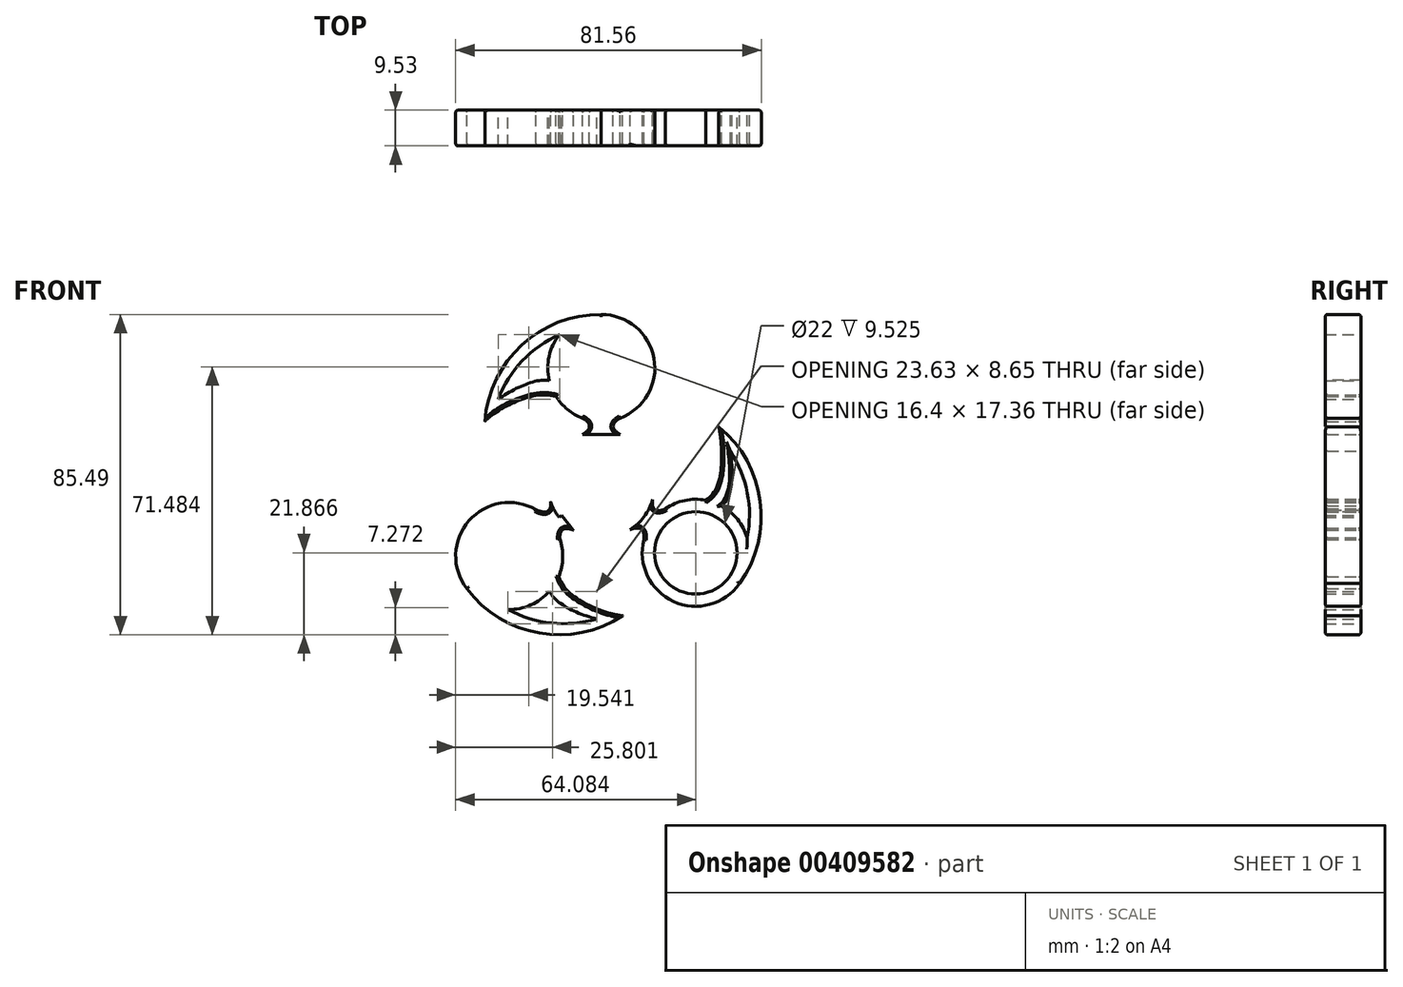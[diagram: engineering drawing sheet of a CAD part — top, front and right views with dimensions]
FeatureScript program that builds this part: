
annotation { "Feature Type Name" : "Feature", "Feature Type Description" : "" }
export const myFeature = defineFeature(function(context is Context, id is Id, definition is map)
    precondition{}
    {
        {
            var Q0;
            Q0=qCreatedBy(makeId("Front.planeOp"),FACE);
            var sketch = newSketch(context, id + "F0", { "sketchPlane" : qUnion([Q0])});
            skCircle(sketch, "E0", {"center": v(0, 0) * mm, "radius": 14.29 * mm});
            skLineSegment(sketch, "E1", {"start": v(0, 0) * mm, "end": v(0, 14.29) * mm});
            skLineSegment(sketch, "E2", {"start": v(0, 0) * mm, "end": v(-11.3, -8.76) * mm});
            skLineSegment(sketch, "E3", {"start": v(0, 0) * mm, "end": v(11.43, -8.57) * mm});
            skCircle(sketch, "E4", {"center": v(0, 31.12) * mm, "radius": 14.29 * mm});
            skLineSegment(sketch, "E5", {"start": v(0, 14.29) * mm, "end": v(0, 16.83) * mm});
            skArc(sketch, "E6", {"start": v(0, 45.4) * mm, "mid": v(-21.2, 37.27) * mm, "end": v(-31.1, 16.83) * mm});
            skFitSpline(sketch, "E7", {"points": [v(-31.1, 16.83) * mm, v(-17.35, 23.79) * mm, v(0, 16.83) * mm], "startDerivative": vector(18.3, 19.68) * mm, "endDerivative": vector(52.34, -33.11) * mm});
            skLineSegment(sketch, "E8", {"start": v(0, 15.56) * mm, "end": v(-3.18, 15.56) * mm});
            skPoint(sketch, "E8.endSnap0", {"position": v(0, 15.56) * mm});
            skLineSegment(sketch, "E9", {"start": v(0, 15.56) * mm, "end": v(3.18, 15.56) * mm});
            skLineSegment(sketch, "E10", {"start": v(0, 17.74) * mm, "end": v(5.03, 17.74) * mm});
            skLineSegment(sketch, "E11", {"start": v(0, 17.74) * mm, "end": v(-5.03, 17.74) * mm});
            skLineSegment(sketch, "E12", {"start": v(0, 14.29) * mm, "end": v(0, 13.37) * mm});
            skLineSegment(sketch, "E13", {"start": v(0, 13.37) * mm, "end": v(-5.03, 13.37) * mm});
            skLineSegment(sketch, "E14", {"start": v(0, 13.37) * mm, "end": v(5.03, 13.37) * mm});
            skFitSpline(sketch, "E15", {"points": [v(-5.03, 17.74) * mm, v(-3.18, 15.56) * mm, v(-5.03, 13.37) * mm], "startDerivative": vector(7.47, -4.37) * mm, "endDerivative": vector(-7.47, -4.37) * mm});
            skFitSpline(sketch, "E16", {"points": [v(5.03, 13.37) * mm, v(3.18, 15.56) * mm, v(5.03, 17.74) * mm], "startDerivative": vector(-7.47, 4.37) * mm, "endDerivative": vector(7.47, 4.37) * mm});
            skArc(sketch, "E17", {"start": v(4.36, 42.56) * mm, "mid": v(-16.61, 36.94) * mm, "end": v(-28.69, 18.9) * mm});
            skFitSpline(sketch, "E18", {"points": [v(-30.7, 19.98) * mm, v(-16.8, 27.72) * mm, v(0.44, 19.97) * mm], "startDerivative": vector(18.3, 19.68) * mm, "endDerivative": vector(52.34, -33.11) * mm});
            skLineSegment(sketch, "E19", {"start": v(-3.18, 15.56) * mm, "end": v(0, 14.29) * mm});
            skLineSegment(sketch, "E20", {"start": v(0, 14.29) * mm, "end": v(3.18, 15.56) * mm});
            skCircle(sketch, "E21", {"center": v(25.21, -18.22) * mm, "radius": 14.29 * mm});
            skLineSegment(sketch, "E22", {"start": v(11.43, -8.57) * mm, "end": v(13.51, -10.03) * mm});
            skArc(sketch, "E23", {"start": v(36.92, -26.42) * mm, "mid": v(42.42, -4.39) * mm, "end": v(31.34, 15.44) * mm});
            skFitSpline(sketch, "E24", {"points": [v(31.34, 15.44) * mm, v(30.71, -0.93) * mm, v(13.51, -10.03) * mm], "startDerivative": vector(5.62, -26.28) * mm, "endDerivative": vector(-57.15, -23.88) * mm});
            skLineSegment(sketch, "E25", {"start": v(12.47, -9.3) * mm, "end": v(14.3, -6.7) * mm});
            skPoint(sketch, "E25.endSnap0", {"position": v(12.47, -9.3) * mm});
            skLineSegment(sketch, "E26", {"start": v(12.47, -9.3) * mm, "end": v(10.65, -11.9) * mm});
            skLineSegment(sketch, "E27", {"start": v(14.26, -10.55) * mm, "end": v(11.38, -14.67) * mm});
            skLineSegment(sketch, "E28", {"start": v(14.26, -10.55) * mm, "end": v(17.14, -6.43) * mm});
            skArc(sketch, "E29", {"start": v(32.04, -28.23) * mm, "mid": v(39.54, -7.93) * mm, "end": v(31.84, 12.3) * mm});
            skFitSpline(sketch, "E30", {"points": [v(33.7, 13.3) * mm, v(33.83, -3.4) * mm, v(15.84, -12.2) * mm], "startDerivative": vector(5.62, -26.28) * mm, "endDerivative": vector(-57.15, -23.88) * mm});
            skLineSegment(sketch, "E31", {"start": v(14.3, -6.7) * mm, "end": v(11.8, -8.05) * mm});
            skLineSegment(sketch, "E32", {"start": v(11.43, -8.57) * mm, "end": v(10.65, -11.9) * mm});
            skLineSegment(sketch, "E33.0", {"start": v(14.3, -6.7) * mm, "end": v(12.47, -9.3) * mm, "construction": true});
            skCircle(sketch, "E34", {"center": v(-24.58, -19.07) * mm, "radius": 14.29 * mm});
            skLineSegment(sketch, "E35", {"start": v(-11.3, -8.76) * mm, "end": v(-13.26, -10.36) * mm});
            skArc(sketch, "E36", {"start": v(-35.91, -27.78) * mm, "mid": v(-16.54, -39.63) * mm, "end": v(5.7, -35.02) * mm});
            skFitSpline(sketch, "E37", {"points": [v(5.7, -35.02) * mm, v(-8.63, -28.76) * mm, v(-13.26, -10.36) * mm], "startDerivative": vector(-26.76, 2.52) * mm, "endDerivative": vector(-5.64, 61.68) * mm});
            skLineSegment(sketch, "E38", {"start": v(-12.27, -9.56) * mm, "end": v(-10.26, -12.02) * mm});
            skPoint(sketch, "E38.endSnap0", {"position": v(-12.27, -9.56) * mm});
            skLineSegment(sketch, "E39", {"start": v(-12.27, -9.56) * mm, "end": v(-14.28, -7.1) * mm});
            skLineSegment(sketch, "E40", {"start": v(-13.97, -10.94) * mm, "end": v(-17.43, -6.7) * mm});
            skLineSegment(sketch, "E41", {"start": v(-13.97, -10.94) * mm, "end": v(-11.04, -14.51) * mm});
            skArc(sketch, "E42", {"start": v(-36.27, -22.58) * mm, "mid": v(-19.07, -35.8) * mm, "end": v(2.57, -34.43) * mm});
            skFitSpline(sketch, "E43", {"points": [v(2.95, -36.62) * mm, v(-12.05, -30.77) * mm, v(-16.16, -11.65) * mm], "startDerivative": vector(-26.76, 2.52) * mm, "endDerivative": vector(-5.64, 61.68) * mm});
            skLineSegment(sketch, "E44", {"start": v(-10.26, -12.02) * mm, "end": v(-10.8, -9.23) * mm});
            skLineSegment(sketch, "E45", {"start": v(-11.3, -8.76) * mm, "end": v(-14.28, -7.1) * mm});
            skLineSegment(sketch, "E46.0", {"start": v(-10.26, -12.02) * mm, "end": v(-12.27, -9.56) * mm, "construction": true});
            skLineSegment(sketch, "E47", {"start": v(-11.3, -8.76) * mm, "end": v(-10.57, -8.2) * mm});
            skLineSegment(sketch, "E48", {"start": v(11.43, -8.57) * mm, "end": v(10.7, -8.02) * mm});
            skLineSegment(sketch, "E49", {"start": v(10.7, -8.02) * mm, "end": v(13.72, -4) * mm});
            skLineSegment(sketch, "E50", {"start": v(10.7, -8.02) * mm, "end": v(7.68, -12.05) * mm});
            skLineSegment(sketch, "E51", {"start": v(-10.57, -8.2) * mm, "end": v(-13.54, -4.56) * mm});
            skLineSegment(sketch, "E52", {"start": v(-10.57, -8.2) * mm, "end": v(-7.49, -12.17) * mm});
            skFitSpline(sketch, "E53", {"points": [v(-13.54, -4.56) * mm, v(-14.28, -7.1) * mm, v(-17.43, -6.7) * mm], "startDerivative": vector(0.73, -8.28) * mm, "endDerivative": vector(-8.38, 3.81) * mm});
            skFitSpline(sketch, "E54", {"points": [v(-11.04, -14.51) * mm, v(-10.26, -12.02) * mm, v(-7.49, -12.17) * mm], "startDerivative": vector(-0.57, 7.9) * mm, "endDerivative": vector(7.64, -3.14) * mm});
            skFitSpline(sketch, "E55", {"points": [v(7.68, -12.05) * mm, v(10.65, -11.9) * mm, v(11.38, -14.67) * mm], "startDerivative": vector(8.1, 3.32) * mm, "endDerivative": vector(-0.74, -8.6) * mm});
            skFitSpline(sketch, "E56", {"points": [v(13.72, -4) * mm, v(14.3, -6.7) * mm, v(17.14, -6.43) * mm], "startDerivative": vector(-1.06, -8.48) * mm, "endDerivative": vector(7.9, 3.59) * mm});
            skSolve(sketch);
        }
        {
            var Q0;
            {var subQ0=sQuery(id+"F0.wireOp",EDGE,"E6");var subQ1=sQuery(id+"F0.wireOp",EDGE,"E4");var subQ2=makeQuery(id+"F0.imprint","INTERSECT",VERTEX,{"derivedFrom":[subQ1,subQ0]});Q0=makeQuery(id+"F0.imprint","IMPRINT",FACE,{"disambiguationData":[TD([[makeQuery(id+"F0.imprint","IMPRINT",EDGE,{"disambiguationData":[TD([[subQ2,-1.0]])],"derivedFrom":subQ1}),-1.0]])]});}
            var Q1;
            {var subQ0=sQuery(id+"F0.wireOp",EDGE,"E18");var subQ1=sQuery(id+"F0.wireOp",EDGE,"E4");var subQ2=makeQuery(id+"F0.imprint","INTERSECT",VERTEX,{"derivedFrom":[subQ1,subQ0]});Q1=makeQuery(id+"F0.imprint","IMPRINT",FACE,{"disambiguationData":[TD([[makeQuery(id+"F0.imprint","IMPRINT",EDGE,{"disambiguationData":[TD([[subQ2,-1.0]])],"derivedFrom":subQ1}),-1.0]])]});}
            var Q2;
            {var subQ0=sQuery(id+"F0.wireOp",EDGE,"E7");var subQ1=sQuery(id+"F0.wireOp",EDGE,"E6");var subQ2=makeQuery(id+"F0.imprint","INTERSECT",VERTEX,{"derivedFrom":[subQ1,subQ0]});Q2=makeQuery(id+"F0.imprint","IMPRINT",FACE,{"disambiguationData":[TD([[makeQuery(id+"F0.imprint","IMPRINT",EDGE,{"disambiguationData":[TD([[subQ2,1.0]])],"derivedFrom":subQ1}),1.0]])]});}
            var Q3;
            {var subQ7=sQuery(id+"F0.wireOp",EDGE,"E10");Q3=makeQuery(id+"F0.imprint","IMPRINT",FACE,{"disambiguationData":[TD([[makeQuery(id+"F0.imprint","IMPRINT",EDGE,{"derivedFrom":subQ7}),1.0]])]});}
            var Q4;
            Q4=makeQuery(id+"F0.imprint","IMPRINT",FACE,{"disambiguationData":[TD([[makeQuery(id+"F0.imprint","IMPRINT",EDGE,{"derivedFrom":sQuery(id+"F0.wireOp",EDGE,"E1")}),1.0]])]});
            var Q5;
            Q5=makeQuery(id+"F0.imprint","IMPRINT",FACE,{"disambiguationData":[TD([[makeQuery(id+"F0.imprint","IMPRINT",EDGE,{"derivedFrom":sQuery(id+"F0.wireOp",EDGE,"E2")}),1.0]])]});
            var Q6;
            Q6=makeQuery(id+"F0.imprint","IMPRINT",FACE,{"disambiguationData":[TD([[makeQuery(id+"F0.imprint","IMPRINT",EDGE,{"derivedFrom":sQuery(id+"F0.wireOp",EDGE,"E1")}),-1.0]])]});
            var Q7;
            {var subQ7=sQuery(id+"F0.wireOp",EDGE,"E40");Q7=makeQuery(id+"F0.imprint","IMPRINT",FACE,{"disambiguationData":[TD([[makeQuery(id+"F0.imprint","IMPRINT",EDGE,{"derivedFrom":subQ7}),1.0]])]});}
            var Q8;
            {var subQ0=sQuery(id+"F0.wireOp",EDGE,"E36");var subQ1=sQuery(id+"F0.wireOp",EDGE,"E34");var subQ2=makeQuery(id+"F0.imprint","INTERSECT",VERTEX,{"derivedFrom":[subQ1,subQ0]});Q8=makeQuery(id+"F0.imprint","IMPRINT",FACE,{"disambiguationData":[TD([[makeQuery(id+"F0.imprint","IMPRINT",EDGE,{"disambiguationData":[TD([[subQ2,-1.0]])],"derivedFrom":subQ1}),-1.0]])]});}
            var Q9;
            {var subQ0=sQuery(id+"F0.wireOp",EDGE,"E43");var subQ1=sQuery(id+"F0.wireOp",EDGE,"E34");var subQ2=makeQuery(id+"F0.imprint","INTERSECT",VERTEX,{"derivedFrom":[subQ1,subQ0]});Q9=makeQuery(id+"F0.imprint","IMPRINT",FACE,{"disambiguationData":[TD([[makeQuery(id+"F0.imprint","IMPRINT",EDGE,{"disambiguationData":[TD([[subQ2,-1.0]])],"derivedFrom":subQ1}),-1.0]])]});}
            var Q10;
            {var subQ0=sQuery(id+"F0.wireOp",EDGE,"E37");var subQ1=sQuery(id+"F0.wireOp",EDGE,"E36");var subQ2=makeQuery(id+"F0.imprint","INTERSECT",VERTEX,{"derivedFrom":[subQ1,subQ0]});Q10=makeQuery(id+"F0.imprint","IMPRINT",FACE,{"disambiguationData":[TD([[makeQuery(id+"F0.imprint","IMPRINT",EDGE,{"disambiguationData":[TD([[subQ2,1.0]])],"derivedFrom":subQ1}),1.0]])]});}
            var Q11;
            {var subQ1=sQuery(id+"F0.wireOp",EDGE,"E34");var subQ3=sQuery(id+"F0.wireOp",EDGE,"E37");var subQ4=makeQuery(id+"F0.imprint","INTERSECT",VERTEX,{"derivedFrom":[subQ1,subQ3]});Q11=makeQuery(id+"F0.imprint","IMPRINT",FACE,{"disambiguationData":[TD([[makeQuery(id+"F0.imprint","IMPRINT",EDGE,{"disambiguationData":[TD([[subQ4,-1.0]])],"derivedFrom":subQ3}),-1.0]])]});}
            var Q12;
            {var subQ5=sQuery(id+"F0.wireOp",EDGE,"E27");Q12=makeQuery(id+"F0.imprint","IMPRINT",FACE,{"disambiguationData":[TD([[makeQuery(id+"F0.imprint","IMPRINT",EDGE,{"derivedFrom":subQ5}),1.0]])]});}
            var Q13;
            {var subQ0=sQuery(id+"F0.wireOp",EDGE,"E23");var subQ1=sQuery(id+"F0.wireOp",EDGE,"E21");var subQ2=makeQuery(id+"F0.imprint","INTERSECT",VERTEX,{"derivedFrom":[subQ1,subQ0]});Q13=makeQuery(id+"F0.imprint","IMPRINT",FACE,{"disambiguationData":[TD([[makeQuery(id+"F0.imprint","IMPRINT",EDGE,{"disambiguationData":[TD([[subQ2,-1.0]])],"derivedFrom":subQ1}),-1.0]])]});}
            var Q14;
            {var subQ0=sQuery(id+"F0.wireOp",EDGE,"E30");var subQ1=sQuery(id+"F0.wireOp",EDGE,"E21");var subQ2=makeQuery(id+"F0.imprint","INTERSECT",VERTEX,{"derivedFrom":[subQ1,subQ0]});Q14=makeQuery(id+"F0.imprint","IMPRINT",FACE,{"disambiguationData":[TD([[makeQuery(id+"F0.imprint","IMPRINT",EDGE,{"disambiguationData":[TD([[subQ2,-1.0]])],"derivedFrom":subQ1}),-1.0]])]});}
            var Q15;
            {var subQ0=sQuery(id+"F0.wireOp",EDGE,"E24");var subQ1=sQuery(id+"F0.wireOp",EDGE,"E23");var subQ2=makeQuery(id+"F0.imprint","INTERSECT",VERTEX,{"derivedFrom":[subQ1,subQ0]});Q15=makeQuery(id+"F0.imprint","IMPRINT",FACE,{"disambiguationData":[TD([[makeQuery(id+"F0.imprint","IMPRINT",EDGE,{"disambiguationData":[TD([[subQ2,1.0]])],"derivedFrom":subQ1}),1.0]])]});}
            var Q16;
            {var subQ0=sQuery(id+"F0.wireOp",EDGE,"E28");var subQ1=sQuery(id+"F0.wireOp",EDGE,"E21");var subQ2=makeQuery(id+"F0.imprint","INTERSECT",VERTEX,{"derivedFrom":[subQ1,subQ0]});Q16=makeQuery(id+"F0.imprint","IMPRINT",FACE,{"disambiguationData":[TD([[makeQuery(id+"F0.imprint","IMPRINT",EDGE,{"disambiguationData":[TD([[subQ2,1.0]])],"derivedFrom":subQ1}),1.0]])]});}
            var Q17;
            {var subQ3=sQuery(id+"F0.wireOp",EDGE,"E40");Q17=makeQuery(id+"F0.imprint","IMPRINT",FACE,{"disambiguationData":[TD([[makeQuery(id+"F0.imprint","IMPRINT",EDGE,{"derivedFrom":subQ3}),-1.0]])]});}
            var Q18;
            {var subQ0=sQuery(id+"F0.wireOp",EDGE,"E37");var subQ3=sQuery(id+"F0.wireOp",EDGE,"E41");var subQ5=makeQuery(id+"F0.imprint","INTERSECT",VERTEX,{"derivedFrom":[subQ0,subQ3]});Q18=makeQuery(id+"F0.imprint","IMPRINT",FACE,{"disambiguationData":[TD([[makeQuery(id+"F0.imprint","IMPRINT",EDGE,{"disambiguationData":[TD([[subQ5,-1.0]])],"derivedFrom":subQ0}),-1.0]])]});}
            var Q19;
            {var subQ0=sQuery(id+"F0.wireOp",EDGE,"E47");Q19=makeQuery(id+"F0.imprint","IMPRINT",FACE,{"disambiguationData":[TD([[makeQuery(id+"F0.imprint","IMPRINT",EDGE,{"derivedFrom":subQ0}),-1.0]])]});}
            var Q20;
            {var subQ0=sQuery(id+"F0.wireOp",EDGE,"E47");Q20=makeQuery(id+"F0.imprint","IMPRINT",FACE,{"disambiguationData":[TD([[makeQuery(id+"F0.imprint","IMPRINT",EDGE,{"derivedFrom":subQ0}),1.0]])]});}
            var Q21;
            {var subQ0=sQuery(id+"F0.wireOp",EDGE,"E45");Q21=makeQuery(id+"F0.imprint","IMPRINT",FACE,{"disambiguationData":[TD([[makeQuery(id+"F0.imprint","IMPRINT",EDGE,{"derivedFrom":subQ0}),-1.0]])]});}
            var Q22;
            {var subQ1=sQuery(id+"F0.wireOp",EDGE,"E0");var subQ3=sQuery(id+"F0.wireOp",EDGE,"E44");var subQ4=makeQuery(id+"F0.imprint","INTERSECT",VERTEX,{"derivedFrom":[subQ1,subQ3]});Q22=makeQuery(id+"F0.imprint","IMPRINT",FACE,{"disambiguationData":[TD([[makeQuery(id+"F0.imprint","IMPRINT",EDGE,{"disambiguationData":[TD([[subQ4,-1.0]])],"derivedFrom":subQ1}),-1.0]])]});}
            var Q23;
            {var subQ5=sQuery(id+"F0.wireOp",EDGE,"E38");Q23=makeQuery(id+"F0.imprint","IMPRINT",FACE,{"disambiguationData":[TD([[makeQuery(id+"F0.imprint","IMPRINT",EDGE,{"derivedFrom":subQ5}),-1.0]])]});}
            var Q24;
            {var subQ5=sQuery(id+"F0.wireOp",EDGE,"E39");Q24=makeQuery(id+"F0.imprint","IMPRINT",FACE,{"disambiguationData":[TD([[makeQuery(id+"F0.imprint","IMPRINT",EDGE,{"derivedFrom":subQ5}),1.0]])]});}
            var Q25;
            {var subQ2=sQuery(id+"F0.wireOp",EDGE,"E39");Q25=makeQuery(id+"F0.imprint","IMPRINT",FACE,{"disambiguationData":[TD([[makeQuery(id+"F0.imprint","IMPRINT",EDGE,{"derivedFrom":subQ2}),-1.0]])]});}
            var Q26;
            {var subQ5=sQuery(id+"F0.wireOp",EDGE,"E38");Q26=makeQuery(id+"F0.imprint","IMPRINT",FACE,{"disambiguationData":[TD([[makeQuery(id+"F0.imprint","IMPRINT",EDGE,{"derivedFrom":subQ5}),1.0]])]});}
            var Q27;
            {var subQ3=sQuery(id+"F0.wireOp",EDGE,"E27");Q27=makeQuery(id+"F0.imprint","IMPRINT",FACE,{"disambiguationData":[TD([[makeQuery(id+"F0.imprint","IMPRINT",EDGE,{"derivedFrom":subQ3}),-1.0]])]});}
            var Q28;
            {var subQ0=sQuery(id+"F0.wireOp",EDGE,"E24");var subQ3=sQuery(id+"F0.wireOp",EDGE,"E28");var subQ5=makeQuery(id+"F0.imprint","INTERSECT",VERTEX,{"derivedFrom":[subQ0,subQ3]});Q28=makeQuery(id+"F0.imprint","IMPRINT",FACE,{"disambiguationData":[TD([[makeQuery(id+"F0.imprint","IMPRINT",EDGE,{"disambiguationData":[TD([[subQ5,-1.0]])],"derivedFrom":subQ0}),-1.0]])]});}
            var Q29;
            {var subQ5=sQuery(id+"F0.wireOp",EDGE,"E25");Q29=makeQuery(id+"F0.imprint","IMPRINT",FACE,{"disambiguationData":[TD([[makeQuery(id+"F0.imprint","IMPRINT",EDGE,{"derivedFrom":subQ5}),-1.0]])]});}
            var Q30;
            {var subQ2=sQuery(id+"F0.wireOp",EDGE,"E25");Q30=makeQuery(id+"F0.imprint","IMPRINT",FACE,{"disambiguationData":[TD([[makeQuery(id+"F0.imprint","IMPRINT",EDGE,{"derivedFrom":subQ2}),1.0]])]});}
            var Q31;
            {var subQ0=sQuery(id+"F0.wireOp",EDGE,"E31");Q31=makeQuery(id+"F0.imprint","IMPRINT",FACE,{"disambiguationData":[TD([[makeQuery(id+"F0.imprint","IMPRINT",EDGE,{"derivedFrom":subQ0}),-1.0]])]});}
            var Q32;
            {var subQ0=sQuery(id+"F0.wireOp",EDGE,"E48");Q32=makeQuery(id+"F0.imprint","IMPRINT",FACE,{"disambiguationData":[TD([[makeQuery(id+"F0.imprint","IMPRINT",EDGE,{"derivedFrom":subQ0}),-1.0]])]});}
            var Q33;
            {var subQ0=sQuery(id+"F0.wireOp",EDGE,"E48");Q33=makeQuery(id+"F0.imprint","IMPRINT",FACE,{"disambiguationData":[TD([[makeQuery(id+"F0.imprint","IMPRINT",EDGE,{"derivedFrom":subQ0}),1.0]])]});}
            var Q34;
            {var subQ0=sQuery(id+"F0.wireOp",EDGE,"E32");Q34=makeQuery(id+"F0.imprint","IMPRINT",FACE,{"disambiguationData":[TD([[makeQuery(id+"F0.imprint","IMPRINT",EDGE,{"derivedFrom":subQ0}),-1.0]])]});}
            var Q35;
            {var subQ2=sQuery(id+"F0.wireOp",EDGE,"E26");Q35=makeQuery(id+"F0.imprint","IMPRINT",FACE,{"disambiguationData":[TD([[makeQuery(id+"F0.imprint","IMPRINT",EDGE,{"derivedFrom":subQ2}),-1.0]])]});}
            var Q36;
            {var subQ5=sQuery(id+"F0.wireOp",EDGE,"E26");Q36=makeQuery(id+"F0.imprint","IMPRINT",FACE,{"disambiguationData":[TD([[makeQuery(id+"F0.imprint","IMPRINT",EDGE,{"derivedFrom":subQ5}),1.0]])]});}
            var Q37;
            {var subQ1=sQuery(id+"F0.wireOp",EDGE,"E4");var subQ3=sQuery(id+"F0.wireOp",EDGE,"E7");var subQ4=makeQuery(id+"F0.imprint","INTERSECT",VERTEX,{"derivedFrom":[subQ1,subQ3]});Q37=makeQuery(id+"F0.imprint","IMPRINT",FACE,{"disambiguationData":[TD([[makeQuery(id+"F0.imprint","IMPRINT",EDGE,{"disambiguationData":[TD([[subQ4,-1.0]])],"derivedFrom":subQ3}),-1.0]])]});}
            var Q38;
            {var subQ0=sQuery(id+"F0.wireOp",EDGE,"E7");var subQ3=sQuery(id+"F0.wireOp",EDGE,"E11");var subQ5=makeQuery(id+"F0.imprint","INTERSECT",VERTEX,{"derivedFrom":[subQ0,subQ3]});Q38=makeQuery(id+"F0.imprint","IMPRINT",FACE,{"disambiguationData":[TD([[makeQuery(id+"F0.imprint","IMPRINT",EDGE,{"disambiguationData":[TD([[subQ5,-1.0]])],"derivedFrom":subQ0}),-1.0]])]});}
            var Q39;
            {var subQ5=sQuery(id+"F0.wireOp",EDGE,"E8");Q39=makeQuery(id+"F0.imprint","IMPRINT",FACE,{"disambiguationData":[TD([[makeQuery(id+"F0.imprint","IMPRINT",EDGE,{"derivedFrom":subQ5}),-1.0]])]});}
            var Q40;
            {var subQ0=sQuery(id+"F0.wireOp",EDGE,"E20");Q40=makeQuery(id+"F0.imprint","IMPRINT",FACE,{"disambiguationData":[TD([[makeQuery(id+"F0.imprint","IMPRINT",EDGE,{"derivedFrom":subQ0}),-1.0]])]});}
            var Q41;
            {var subQ0=sQuery(id+"F0.wireOp",EDGE,"E12");Q41=makeQuery(id+"F0.imprint","IMPRINT",FACE,{"disambiguationData":[TD([[makeQuery(id+"F0.imprint","IMPRINT",EDGE,{"derivedFrom":subQ0}),1.0]])]});}
            var Q42;
            {var subQ0=sQuery(id+"F0.wireOp",EDGE,"E12");Q42=makeQuery(id+"F0.imprint","IMPRINT",FACE,{"disambiguationData":[TD([[makeQuery(id+"F0.imprint","IMPRINT",EDGE,{"derivedFrom":subQ0}),-1.0]])]});}
            var Q43;
            {var subQ0=sQuery(id+"F0.wireOp",EDGE,"E19");Q43=makeQuery(id+"F0.imprint","IMPRINT",FACE,{"disambiguationData":[TD([[makeQuery(id+"F0.imprint","IMPRINT",EDGE,{"derivedFrom":subQ0}),-1.0]])]});}
            var Q44;
            {var subQ2=sQuery(id+"F0.wireOp",EDGE,"E8");Q44=makeQuery(id+"F0.imprint","IMPRINT",FACE,{"disambiguationData":[TD([[makeQuery(id+"F0.imprint","IMPRINT",EDGE,{"derivedFrom":subQ2}),1.0]])]});}
            var Q45;
            {var subQ2=sQuery(id+"F0.wireOp",EDGE,"E9");Q45=makeQuery(id+"F0.imprint","IMPRINT",FACE,{"disambiguationData":[TD([[makeQuery(id+"F0.imprint","IMPRINT",EDGE,{"derivedFrom":subQ2}),-1.0]])]});}
            var Q46;
            {var subQ5=sQuery(id+"F0.wireOp",EDGE,"E9");Q46=makeQuery(id+"F0.imprint","IMPRINT",FACE,{"disambiguationData":[TD([[makeQuery(id+"F0.imprint","IMPRINT",EDGE,{"derivedFrom":subQ5}),1.0]])]});}
            var Q47;
            {var subQ3=sQuery(id+"F0.wireOp",EDGE,"E10");Q47=makeQuery(id+"F0.imprint","IMPRINT",FACE,{"disambiguationData":[TD([[makeQuery(id+"F0.imprint","IMPRINT",EDGE,{"derivedFrom":subQ3}),-1.0]])]});}
            extrude(context, id + "F1", {"entities" : qUnion([Q0, Q1, Q2, Q3, Q4, Q5, Q6, Q7, Q8, Q9, Q10, Q11, Q12, Q13, Q14, Q15, Q16, Q17, Q18, Q19, Q20, Q21, Q22, Q23, Q24, Q25, Q26, Q27, Q28, Q29, Q30, Q31, Q32, Q33, Q34, Q35, Q36, Q37, Q38, Q39, Q40, Q41, Q42, Q43, Q44, Q45, Q46, Q47]), "depth" : 9.52 * mm});
        }
        {
            var Q0;
            {var subQ0=sQuery(id+"F0.wireOp",EDGE,"E4");Q0=makeQuery(id+"F1.opExtrude","CAP_EDGE",EDGE,{"disambiguationData":[OSD([subQ0]),TDD([makeQuery(id+"F0.imprint","IMPRINT",EDGE,{"disambiguationData":[TD([[makeQuery(id+"F0.imprint","INTERSECT",VERTEX,{"derivedFrom":[subQ0,sQuery(id+"F0.wireOp",EDGE,"E7")]}),-1.0]])],"derivedFrom":subQ0})])],"isStart":false});}
            var Q1;
            Q1=makeQuery(id+"F1.opExtrude","CAP_EDGE",EDGE,{"disambiguationData":[OSD([sQuery(id+"F0.wireOp",EDGE,"E15")])],"isStart":false});
            var Q2;
            {var subQ0=sQuery(id+"F0.wireOp",EDGE,"E0");Q2=makeQuery(id+"F1.opExtrude","CAP_EDGE",EDGE,{"disambiguationData":[OSD([subQ0]),TDD([makeQuery(id+"F0.imprint","IMPRINT",EDGE,{"disambiguationData":[TD([[makeQuery(id+"F0.imprint","INTERSECT",VERTEX,{"derivedFrom":[subQ0,sQuery(id+"F0.wireOp",EDGE,"E13"),sQuery(id+"F0.wireOp",EDGE,"E15")]}),-1.0]])],"derivedFrom":subQ0})])],"isStart":false});}
            var Q3;
            Q3=makeQuery(id+"F1.opExtrude","CAP_EDGE",EDGE,{"disambiguationData":[OSD([sQuery(id+"F0.wireOp",EDGE,"E53")])],"isStart":false});
            var Q4;
            {var subQ0=sQuery(id+"F0.wireOp",EDGE,"E34");Q4=makeQuery(id+"F1.opExtrude","CAP_EDGE",EDGE,{"disambiguationData":[OSD([subQ0]),TDD([makeQuery(id+"F0.imprint","IMPRINT",EDGE,{"disambiguationData":[TD([[makeQuery(id+"F0.imprint","INTERSECT",VERTEX,{"derivedFrom":[subQ0,sQuery(id+"F0.wireOp",EDGE,"E36")]}),1.0]])],"derivedFrom":subQ0})])],"isStart":false});}
            var Q5;
            Q5=makeQuery(id+"F1.opExtrude","CAP_EDGE",EDGE,{"disambiguationData":[OSD([sQuery(id+"F0.wireOp",EDGE,"E36")])],"isStart":false});
            var Q6;
            Q6=makeQuery(id+"F1.opExtrude","CAP_EDGE",EDGE,{"disambiguationData":[OSD([sQuery(id+"F0.wireOp",EDGE,"E37")])],"isStart":false});
            var Q7;
            Q7=makeQuery(id+"F1.opExtrude","CAP_FACE",FACE,{"disambiguationData":[OSD([sQuery(id+"F0.wireOp",EDGE,"E0"),sQuery(id+"F0.wireOp",EDGE,"E4"),sQuery(id+"F0.wireOp",EDGE,"E6"),sQuery(id+"F0.wireOp",EDGE,"E7"),sQuery(id+"F0.wireOp",EDGE,"E15"),sQuery(id+"F0.wireOp",EDGE,"E16"),sQuery(id+"F0.wireOp",EDGE,"E17"),sQuery(id+"F0.wireOp",EDGE,"E18"),sQuery(id+"F0.wireOp",EDGE,"E21"),sQuery(id+"F0.wireOp",EDGE,"E23"),sQuery(id+"F0.wireOp",EDGE,"E24"),sQuery(id+"F0.wireOp",EDGE,"E29"),sQuery(id+"F0.wireOp",EDGE,"E30"),sQuery(id+"F0.wireOp",EDGE,"E34"),sQuery(id+"F0.wireOp",EDGE,"E36"),sQuery(id+"F0.wireOp",EDGE,"E37"),sQuery(id+"F0.wireOp",EDGE,"E42"),sQuery(id+"F0.wireOp",EDGE,"E43"),sQuery(id+"F0.wireOp",EDGE,"E53"),sQuery(id+"F0.wireOp",EDGE,"E54"),sQuery(id+"F0.wireOp",EDGE,"E55"),sQuery(id+"F0.wireOp",EDGE,"E56")])],"isStart":false});
            var Q8;
            Q8=makeQuery(id+"F1.opExtrude","CAP_EDGE",EDGE,{"disambiguationData":[OSD([sQuery(id+"F0.wireOp",EDGE,"E7")])],"isStart":false});
            var Q9;
            Q9=makeQuery(id+"F1.opExtrude","CAP_EDGE",EDGE,{"disambiguationData":[OSD([sQuery(id+"F0.wireOp",EDGE,"E54")])],"isStart":false});
            var Q10;
            {var subQ0=sQuery(id+"F0.wireOp",EDGE,"E34");Q10=makeQuery(id+"F1.opExtrude","CAP_EDGE",EDGE,{"disambiguationData":[OSD([subQ0]),TDD([makeQuery(id+"F0.imprint","IMPRINT",EDGE,{"disambiguationData":[TD([[makeQuery(id+"F0.imprint","INTERSECT",VERTEX,{"derivedFrom":[subQ0,sQuery(id+"F0.wireOp",EDGE,"E37")]}),-1.0]])],"derivedFrom":subQ0})])],"isStart":false});}
            var Q11;
            {var subQ0=sQuery(id+"F0.wireOp",EDGE,"E0");Q11=makeQuery(id+"F1.opExtrude","CAP_EDGE",EDGE,{"disambiguationData":[OSD([subQ0]),TDD([makeQuery(id+"F0.imprint","IMPRINT",EDGE,{"disambiguationData":[TD([[makeQuery(id+"F0.imprint","INTERSECT",VERTEX,{"derivedFrom":[subQ0,sQuery(id+"F0.wireOp",EDGE,"E50"),sQuery(id+"F0.wireOp",EDGE,"E55")]}),1.0]])],"derivedFrom":subQ0})])],"isStart":false});}
            var Q12;
            Q12=makeQuery(id+"F1.opExtrude","CAP_EDGE",EDGE,{"disambiguationData":[OSD([sQuery(id+"F0.wireOp",EDGE,"E55")])],"isStart":false});
            var Q13;
            {var subQ0=sQuery(id+"F0.wireOp",EDGE,"E21");Q13=makeQuery(id+"F1.opExtrude","CAP_EDGE",EDGE,{"disambiguationData":[OSD([subQ0]),TDD([makeQuery(id+"F0.imprint","IMPRINT",EDGE,{"disambiguationData":[TD([[makeQuery(id+"F0.imprint","INTERSECT",VERTEX,{"derivedFrom":[subQ0,sQuery(id+"F0.wireOp",EDGE,"E23")]}),1.0]])],"derivedFrom":subQ0})])],"isStart":false});}
            var Q14;
            Q14=makeQuery(id+"F1.opExtrude","CAP_EDGE",EDGE,{"disambiguationData":[OSD([sQuery(id+"F0.wireOp",EDGE,"E23")])],"isStart":false});
            var Q15;
            Q15=makeQuery(id+"F1.opExtrude","CAP_EDGE",EDGE,{"disambiguationData":[OSD([sQuery(id+"F0.wireOp",EDGE,"E24")])],"isStart":false});
            var Q16;
            {var subQ0=sQuery(id+"F0.wireOp",EDGE,"E21");Q16=makeQuery(id+"F1.opExtrude","CAP_EDGE",EDGE,{"disambiguationData":[OSD([subQ0]),TDD([makeQuery(id+"F0.imprint","IMPRINT",EDGE,{"disambiguationData":[TD([[makeQuery(id+"F0.imprint","INTERSECT",VERTEX,{"derivedFrom":[subQ0,sQuery(id+"F0.wireOp",EDGE,"E24")]}),-1.0]])],"derivedFrom":subQ0})])],"isStart":false});}
            var Q17;
            Q17=makeQuery(id+"F1.opExtrude","CAP_EDGE",EDGE,{"disambiguationData":[OSD([sQuery(id+"F0.wireOp",EDGE,"E56")])],"isStart":false});
            var Q18;
            {var subQ0=sQuery(id+"F0.wireOp",EDGE,"E0");Q18=makeQuery(id+"F1.opExtrude","CAP_EDGE",EDGE,{"disambiguationData":[OSD([subQ0]),TDD([makeQuery(id+"F0.imprint","IMPRINT",EDGE,{"disambiguationData":[TD([[makeQuery(id+"F0.imprint","INTERSECT",VERTEX,{"derivedFrom":[subQ0,sQuery(id+"F0.wireOp",EDGE,"E14"),sQuery(id+"F0.wireOp",EDGE,"E16")]}),1.0]])],"derivedFrom":subQ0})])],"isStart":false});}
            var Q19;
            Q19=makeQuery(id+"F1.opExtrude","CAP_EDGE",EDGE,{"disambiguationData":[OSD([sQuery(id+"F0.wireOp",EDGE,"E16")])],"isStart":false});
            var Q20;
            {var subQ0=sQuery(id+"F0.wireOp",EDGE,"E4");Q20=makeQuery(id+"F1.opExtrude","CAP_EDGE",EDGE,{"disambiguationData":[OSD([subQ0]),TDD([makeQuery(id+"F0.imprint","IMPRINT",EDGE,{"disambiguationData":[TD([[makeQuery(id+"F0.imprint","INTERSECT",VERTEX,{"derivedFrom":[subQ0,sQuery(id+"F0.wireOp",EDGE,"E6")]}),1.0]])],"derivedFrom":subQ0})])],"isStart":false});}
            var Q21;
            Q21=makeQuery(id+"F1.opExtrude","CAP_EDGE",EDGE,{"disambiguationData":[OSD([sQuery(id+"F0.wireOp",EDGE,"E6")])],"isStart":false});
            var Q22;
            Q22=makeQuery(id+"F1.opExtrude","CAP_EDGE",EDGE,{"disambiguationData":[OSD([sQuery(id+"F0.wireOp",EDGE,"E16")])],"isStart":true});
            var Q23;
            {var subQ0=sQuery(id+"F0.wireOp",EDGE,"E4");Q23=makeQuery(id+"F1.opExtrude","CAP_EDGE",EDGE,{"disambiguationData":[OSD([subQ0]),TDD([makeQuery(id+"F0.imprint","IMPRINT",EDGE,{"disambiguationData":[TD([[makeQuery(id+"F0.imprint","INTERSECT",VERTEX,{"derivedFrom":[subQ0,sQuery(id+"F0.wireOp",EDGE,"E6")]}),1.0]])],"derivedFrom":subQ0})])],"isStart":true});}
            var Q24;
            {var subQ0=sQuery(id+"F0.wireOp",EDGE,"E0");Q24=makeQuery(id+"F1.opExtrude","CAP_EDGE",EDGE,{"disambiguationData":[OSD([subQ0]),TDD([makeQuery(id+"F0.imprint","IMPRINT",EDGE,{"disambiguationData":[TD([[makeQuery(id+"F0.imprint","INTERSECT",VERTEX,{"derivedFrom":[subQ0,sQuery(id+"F0.wireOp",EDGE,"E14"),sQuery(id+"F0.wireOp",EDGE,"E16")]}),1.0]])],"derivedFrom":subQ0})])],"isStart":true});}
            var Q25;
            Q25=makeQuery(id+"F1.opExtrude","CAP_EDGE",EDGE,{"disambiguationData":[OSD([sQuery(id+"F0.wireOp",EDGE,"E56")])],"isStart":true});
            var Q26;
            {var subQ0=sQuery(id+"F0.wireOp",EDGE,"E21");Q26=makeQuery(id+"F1.opExtrude","CAP_EDGE",EDGE,{"disambiguationData":[OSD([subQ0]),TDD([makeQuery(id+"F0.imprint","IMPRINT",EDGE,{"disambiguationData":[TD([[makeQuery(id+"F0.imprint","INTERSECT",VERTEX,{"derivedFrom":[subQ0,sQuery(id+"F0.wireOp",EDGE,"E24")]}),-1.0]])],"derivedFrom":subQ0})])],"isStart":true});}
            var Q27;
            Q27=makeQuery(id+"F1.opExtrude","CAP_EDGE",EDGE,{"disambiguationData":[OSD([sQuery(id+"F0.wireOp",EDGE,"E23")])],"isStart":true});
            var Q28;
            Q28=makeQuery(id+"F1.opExtrude","CAP_EDGE",EDGE,{"disambiguationData":[OSD([sQuery(id+"F0.wireOp",EDGE,"E55")])],"isStart":true});
            var Q29;
            {var subQ0=sQuery(id+"F0.wireOp",EDGE,"E0");Q29=makeQuery(id+"F1.opExtrude","CAP_EDGE",EDGE,{"disambiguationData":[OSD([subQ0]),TDD([makeQuery(id+"F0.imprint","IMPRINT",EDGE,{"disambiguationData":[TD([[makeQuery(id+"F0.imprint","INTERSECT",VERTEX,{"derivedFrom":[subQ0,sQuery(id+"F0.wireOp",EDGE,"E50"),sQuery(id+"F0.wireOp",EDGE,"E55")]}),1.0]])],"derivedFrom":subQ0})])],"isStart":true});}
            var Q30;
            Q30=makeQuery(id+"F1.opExtrude","CAP_EDGE",EDGE,{"disambiguationData":[OSD([sQuery(id+"F0.wireOp",EDGE,"E54")])],"isStart":true});
            var Q31;
            {var subQ0=sQuery(id+"F0.wireOp",EDGE,"E34");Q31=makeQuery(id+"F1.opExtrude","CAP_EDGE",EDGE,{"disambiguationData":[OSD([subQ0]),TDD([makeQuery(id+"F0.imprint","IMPRINT",EDGE,{"disambiguationData":[TD([[makeQuery(id+"F0.imprint","INTERSECT",VERTEX,{"derivedFrom":[subQ0,sQuery(id+"F0.wireOp",EDGE,"E37")]}),-1.0]])],"derivedFrom":subQ0})])],"isStart":true});}
            var Q32;
            Q32=makeQuery(id+"F1.opExtrude","CAP_EDGE",EDGE,{"disambiguationData":[OSD([sQuery(id+"F0.wireOp",EDGE,"E37")])],"isStart":true});
            var Q33;
            Q33=makeQuery(id+"F1.opExtrude","CAP_EDGE",EDGE,{"disambiguationData":[OSD([sQuery(id+"F0.wireOp",EDGE,"E36")])],"isStart":true});
            var Q34;
            Q34=makeQuery(id+"F1.opExtrude","CAP_EDGE",EDGE,{"disambiguationData":[OSD([sQuery(id+"F0.wireOp",EDGE,"E36")])],"isStart":true});
            var Q35;
            {var subQ0=sQuery(id+"F0.wireOp",EDGE,"E34");Q35=makeQuery(id+"F1.opExtrude","CAP_EDGE",EDGE,{"disambiguationData":[OSD([subQ0]),TDD([makeQuery(id+"F0.imprint","IMPRINT",EDGE,{"disambiguationData":[TD([[makeQuery(id+"F0.imprint","INTERSECT",VERTEX,{"derivedFrom":[subQ0,sQuery(id+"F0.wireOp",EDGE,"E36")]}),1.0]])],"derivedFrom":subQ0})])],"isStart":true});}
            var Q36;
            Q36=makeQuery(id+"F1.opExtrude","CAP_EDGE",EDGE,{"disambiguationData":[OSD([sQuery(id+"F0.wireOp",EDGE,"E53")])],"isStart":true});
            var Q37;
            {var subQ0=sQuery(id+"F0.wireOp",EDGE,"E0");Q37=makeQuery(id+"F1.opExtrude","CAP_EDGE",EDGE,{"disambiguationData":[OSD([subQ0]),TDD([makeQuery(id+"F0.imprint","IMPRINT",EDGE,{"disambiguationData":[TD([[makeQuery(id+"F0.imprint","INTERSECT",VERTEX,{"derivedFrom":[subQ0,sQuery(id+"F0.wireOp",EDGE,"E13"),sQuery(id+"F0.wireOp",EDGE,"E15")]}),-1.0]])],"derivedFrom":subQ0})])],"isStart":true});}
            var Q38;
            Q38=makeQuery(id+"F1.opExtrude","CAP_EDGE",EDGE,{"disambiguationData":[OSD([sQuery(id+"F0.wireOp",EDGE,"E15")])],"isStart":true});
            var Q39;
            {var subQ0=sQuery(id+"F0.wireOp",EDGE,"E4");Q39=makeQuery(id+"F1.opExtrude","CAP_EDGE",EDGE,{"disambiguationData":[OSD([subQ0]),TDD([makeQuery(id+"F0.imprint","IMPRINT",EDGE,{"disambiguationData":[TD([[makeQuery(id+"F0.imprint","INTERSECT",VERTEX,{"derivedFrom":[subQ0,sQuery(id+"F0.wireOp",EDGE,"E7")]}),-1.0]])],"derivedFrom":subQ0})])],"isStart":true});}
            var Q40;
            Q40=makeQuery(id+"F1.opExtrude","CAP_EDGE",EDGE,{"disambiguationData":[OSD([sQuery(id+"F0.wireOp",EDGE,"E7")])],"isStart":true});
            var Q41;
            Q41=makeQuery(id+"F1.opExtrude","CAP_EDGE",EDGE,{"disambiguationData":[OSD([sQuery(id+"F0.wireOp",EDGE,"E6")])],"isStart":true});
            var Q42;
            {var subQ0=sQuery(id+"F0.wireOp",EDGE,"E21");Q42=makeQuery(id+"F1.opExtrude","CAP_EDGE",EDGE,{"disambiguationData":[OSD([subQ0]),TDD([makeQuery(id+"F0.imprint","IMPRINT",EDGE,{"disambiguationData":[TD([[makeQuery(id+"F0.imprint","INTERSECT",VERTEX,{"derivedFrom":[subQ0,sQuery(id+"F0.wireOp",EDGE,"E23")]}),1.0]])],"derivedFrom":subQ0})])],"isStart":true});}
            var Q43;
            Q43=makeQuery(id+"F1.opExtrude","CAP_EDGE",EDGE,{"disambiguationData":[OSD([sQuery(id+"F0.wireOp",EDGE,"E24")])],"isStart":true});
            fillet(context, id + "F2", {"entities" : qUnion([Q0, Q1, Q2, Q3, Q4, Q5, Q6, Q7, Q8, Q9, Q10, Q11, Q12, Q13, Q14, Q15, Q16, Q17, Q18, Q19, Q20, Q21, Q22, Q23, Q24, Q25, Q26, Q27, Q28, Q29, Q30, Q31, Q32, Q33, Q34, Q35, Q36, Q37, Q38, Q39, Q40, Q41, Q42, Q43]), "radius" : 0.64 * mm, "tangentPropagation" : true, "allowEdgeOverflow" : false});
        }
        {
            var Q0;
            Q0=sQuery(id+"F0.wireOp",VERTEX,"E3.start");
            var Q1;
            Q1=sQuery(id+"F0.wireOp",VERTEX,"E4.center");
            var Q2;
            Q2=sQuery(id+"F0.wireOp",VERTEX,"E34.center");
            var Q3;
            Q3=sQuery(id+"F0.wireOp",VERTEX,"E21.center");
            var Q4;
            Q4=makeQuery(id+"F1.opExtrude","SWEPT_BODY",BODY,{"disambiguationData":[OSD([sQuery(id+"F0.wireOp",EDGE,"E0"),sQuery(id+"F0.wireOp",EDGE,"E4"),sQuery(id+"F0.wireOp",EDGE,"E6"),sQuery(id+"F0.wireOp",EDGE,"E7"),sQuery(id+"F0.wireOp",EDGE,"E15"),sQuery(id+"F0.wireOp",EDGE,"E16"),sQuery(id+"F0.wireOp",EDGE,"E17"),sQuery(id+"F0.wireOp",EDGE,"E18"),sQuery(id+"F0.wireOp",EDGE,"E21"),sQuery(id+"F0.wireOp",EDGE,"E23"),sQuery(id+"F0.wireOp",EDGE,"E24"),sQuery(id+"F0.wireOp",EDGE,"E29"),sQuery(id+"F0.wireOp",EDGE,"E30"),sQuery(id+"F0.wireOp",EDGE,"E34"),sQuery(id+"F0.wireOp",EDGE,"E36"),sQuery(id+"F0.wireOp",EDGE,"E37"),sQuery(id+"F0.wireOp",EDGE,"E42"),sQuery(id+"F0.wireOp",EDGE,"E43"),sQuery(id+"F0.wireOp",EDGE,"E53"),sQuery(id+"F0.wireOp",EDGE,"E54"),sQuery(id+"F0.wireOp",EDGE,"E55"),sQuery(id+"F0.wireOp",EDGE,"E56")])]});
            hole(context, id + "F3", {"style" : HoleStyle.SIMPLE, "endStyle" : HoleEndStyle.THROUGH, "oppositeDirection" : true, "holeDiameter" : 22 * mm, "isTappedThrough" : true, "tappedDepth" : 12.7 * mm, "tapClearance" : 3, "locations" : qUnion([Q0, Q1, Q2, Q3]), "scope" : qUnion([Q4])});
        }
    });
